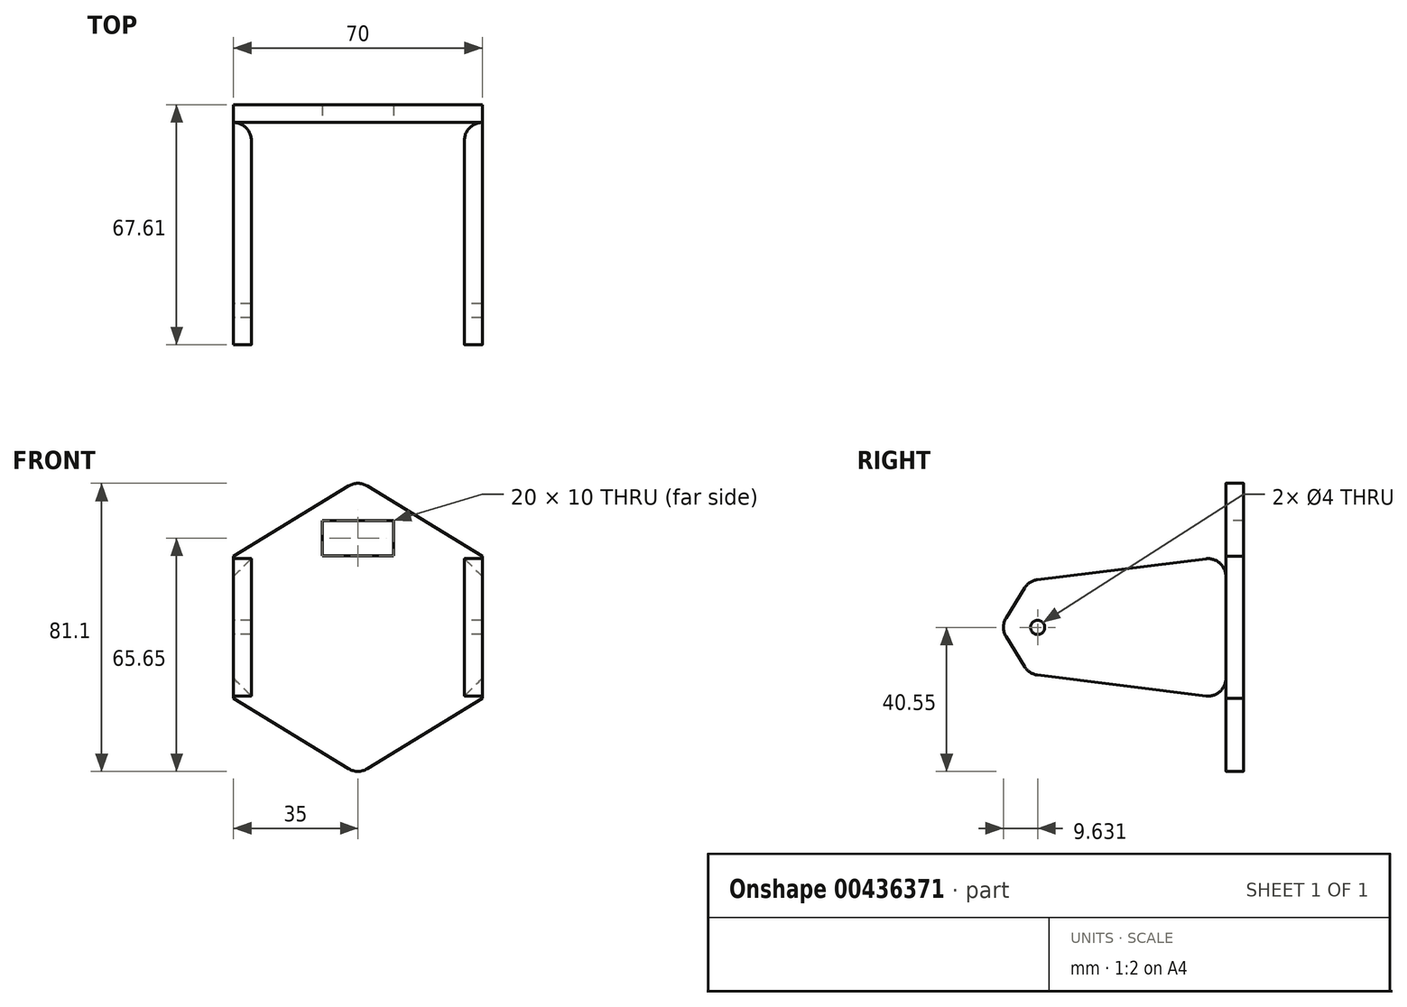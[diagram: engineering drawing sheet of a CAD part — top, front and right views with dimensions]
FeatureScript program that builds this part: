
annotation { "Feature Type Name" : "Feature", "Feature Type Description" : "" }
export const myFeature = defineFeature(function(context is Context, id is Id, definition is map)
    precondition{}
    {
        {
            var Q0;
            Q0=qCreatedBy(makeId("Front.planeOp"),FACE);
            var sketch = newSketch(context, id + "F0", { "sketchPlane" : qUnion([Q0])});
            skLineSegment(sketch, "E0.bottom", {"start": v(-35, 20) * mm, "end": v(-30, 20) * mm});
            skLineSegment(sketch, "E0.top", {"start": v(-35, -20) * mm, "end": v(-30, -20) * mm});
            skLineSegment(sketch, "E0.left", {"start": v(-35, 20) * mm, "end": v(-35, -20) * mm});
            skLineSegment(sketch, "E0.right", {"start": v(-30, 20) * mm, "end": v(-30, -20) * mm});
            skLineSegment(sketch, "E1.MirrorCS", {"start": v(35, 20) * mm, "end": v(30, 20) * mm});
            skLineSegment(sketch, "E2.MirrorCS", {"start": v(35, -20) * mm, "end": v(30, -20) * mm});
            skLineSegment(sketch, "E3.MirrorCS", {"start": v(30, 20) * mm, "end": v(30, -20) * mm});
            skLineSegment(sketch, "E4.MirrorCS", {"start": v(35, 20) * mm, "end": v(35, -20) * mm});
            skSolve(sketch);
        }
        {
            var Q0;
            Q0 = qSketchRegion(id + "F0", true);
            extrude(context, id + "F1", {"entities" : qUnion([Q0]), "depth" : 70 * mm});
        }
        {
            var Q0;
            Q0=makeQuery(id+"F1.opExtrude","CAP_FACE",FACE,{"disambiguationData":[OSD([sQuery(id+"F0.wireOp",EDGE,"E0.bottom"),sQuery(id+"F0.wireOp",EDGE,"E0.top"),sQuery(id+"F0.wireOp",EDGE,"E0.left"),sQuery(id+"F0.wireOp",EDGE,"E0.right")])],"isStart":true});
            var sketch = newSketch(context, id + "F2", { "sketchPlane" : qUnion([Q0])});
            skLineSegment(sketch, "E5", {"start": v(0, -41.41) * mm, "end": v(35, -20) * mm});
            skLineSegment(sketch, "E6.0", {"start": v(35, 20) * mm, "end": v(35, -20) * mm});
            skLineSegment(sketch, "E7.0", {"start": v(-35, 20) * mm, "end": v(-35, -20) * mm});
            skLineSegment(sketch, "E8.MirrorCS", {"start": v(0, -41.41) * mm, "end": v(-35, -20) * mm});
            skLineSegment(sketch, "E9.MirrorCS", {"start": v(0, 41.41) * mm, "end": v(35, 20) * mm});
            skLineSegment(sketch, "E10.MirrorCS", {"start": v(0, 41.41) * mm, "end": v(-35, 20) * mm});
            skSolve(sketch);
        }
        {
            var Q0;
            Q0 = qSketchRegion(id + "F2", true);
            extrude(context, id + "F3", {"entities" : qUnion([Q0]), "depth" : 5 * mm});
        }
        {
            var Q0;
            Q0=makeQuery(id+"F1.opExtrude","SWEPT_FACE",FACE,{"disambiguationData":[OSD([sQuery(id+"F0.wireOp",EDGE,"E0.left")])]});
            var sketch = newSketch(context, id + "F4", { "sketchPlane" : qUnion([Q0])});
            skCircle(sketch, "E11", {"center": v(52.98, 0) * mm, "radius": 2 * mm});
            skSolve(sketch);
        }
        {
            var Q0;
            Q0 = qSketchRegion(id + "F4", true);
            extrude(context, id + "F5", {"entities" : qUnion([Q0]), "operationType" : NewBodyOperationType.REMOVE, "oppositeDirection" : true, "depth" : 97.2 * mm});
        }
        {
            var Q0;
            Q0=makeQuery(id+"F1.opExtrude","SWEPT_FACE",FACE,{"disambiguationData":[OSD([sQuery(id+"F0.wireOp",EDGE,"E0.left")])]});
            var sketch = newSketch(context, id + "F6", { "sketchPlane" : qUnion([Q0])});
            skLineSegment(sketch, "E12", {"start": v(0, 20) * mm, "end": v(53.02, 13.43) * mm});
            skLineSegment(sketch, "E13", {"start": v(56.66, 11.08) * mm, "end": v(61.87, 2.62) * mm});
            skLineSegment(sketch, "E14.MirrorCS", {"start": v(56.66, -11.08) * mm, "end": v(61.87, -2.62) * mm});
            skLineSegment(sketch, "E15.MirrorCS", {"start": v(0, -20) * mm, "end": v(53.02, -13.43) * mm});
            skPoint(sketch, "E16.visualSharp", {"position": v(63.48, 0) * mm});
            skArc(sketch, "E16.filletArc", {"start": v(61.87, -2.62) * mm, "mid": v(62.61, 0) * mm, "end": v(61.87, 2.62) * mm});
            skPoint(sketch, "E17.visualSharp", {"position": v(55.4, 13.13) * mm});
            skArc(sketch, "E17.filletArc", {"start": v(56.66, 11.08) * mm, "mid": v(55.1, 12.67) * mm, "end": v(53.02, 13.43) * mm});
            skPoint(sketch, "E18.visualSharp", {"position": v(55.4, -13.13) * mm});
            skArc(sketch, "E18.filletArc", {"start": v(53.02, -13.43) * mm, "mid": v(55.1, -12.67) * mm, "end": v(56.66, -11.08) * mm});
            skLineSegment(sketch, "E19", {"start": v(0, 20) * mm, "end": v(98.43, 40.8) * mm});
            skLineSegment(sketch, "E20", {"start": v(98.43, 40.8) * mm, "end": v(98.43, -42.02) * mm});
            skLineSegment(sketch, "E21", {"start": v(98.43, -42.02) * mm, "end": v(0, -20) * mm});
            skSolve(sketch);
        }
        {
            var Q0;
            Q0 = qSketchRegion(id + "F6", true);
            extrude(context, id + "F7", {"entities" : qUnion([Q0]), "operationType" : NewBodyOperationType.REMOVE, "oppositeDirection" : true, "depth" : 83.6 * mm});
        }
        {
            var Q0;
            Q0=makeQuery(id+"F3.opExtrude","SWEPT_EDGE",EDGE,{"disambiguationData":[OSD([sQuery(id+"F2.wireOp",EDGE,"E9.MirrorCS"),sQuery(id+"F2.wireOp",EDGE,"E10.MirrorCS")])]});
            var Q1;
            Q1=makeQuery(id+"F1.opExtrude","CAP_EDGE",EDGE,{"disambiguationData":[OSD([sQuery(id+"F0.wireOp",EDGE,"E3.MirrorCS")])],"isStart":true});
            var Q2;
            Q2=makeQuery(id+"F1.opExtrude","CAP_EDGE",EDGE,{"disambiguationData":[OSD([sQuery(id+"F0.wireOp",EDGE,"E0.right")])],"isStart":true});
            var Q3;
            Q3=makeQuery(id+"F3.opExtrude","SWEPT_EDGE",EDGE,{"disambiguationData":[OSD([sQuery(id+"F2.wireOp",EDGE,"E5"),sQuery(id+"F2.wireOp",EDGE,"E8.MirrorCS")])]});
            var Q4;
            Q4=makeQuery(id+"F7.boolean.opBoolean","MERGE",EDGE,{"derivedFrom":[makeQuery(id+"F1.opExtrude","CAP_EDGE",EDGE,{"disambiguationData":[OSD([sQuery(id+"F0.wireOp",EDGE,"E1.MirrorCS")])],"isStart":true}),makeQuery(id+"F7.opExtrude","SWEPT_EDGE",EDGE,{"disambiguationData":[OSD([sQuery(id+"F0.wireOp",EDGE,"E0.bottom"),sQuery(id+"F0.wireOp",EDGE,"E0.left"),sQuery(id+"F6.wireOp",EDGE,"E12"),sQuery(id+"F6.wireOp",EDGE,"E19")])]})]});
            var Q5;
            {var subQ0=sQuery(id+"F0.wireOp",EDGE,"E0.bottom");Q5=makeQuery(id+"F7.boolean.opBoolean","MERGE",EDGE,{"derivedFrom":[makeQuery(id+"F1.opExtrude","CAP_EDGE",EDGE,{"disambiguationData":[OSD([subQ0])],"isStart":true}),makeQuery(id+"F7.opExtrude","SWEPT_EDGE",EDGE,{"disambiguationData":[OSD([subQ0,sQuery(id+"F0.wireOp",EDGE,"E0.left"),sQuery(id+"F6.wireOp",EDGE,"E12"),sQuery(id+"F6.wireOp",EDGE,"E19")])]})]});}
            var Q6;
            {var subQ0=sQuery(id+"F0.wireOp",EDGE,"E0.top");Q6=makeQuery(id+"F7.boolean.opBoolean","MERGE",EDGE,{"derivedFrom":[makeQuery(id+"F1.opExtrude","CAP_EDGE",EDGE,{"disambiguationData":[OSD([subQ0])],"isStart":true}),makeQuery(id+"F7.opExtrude","SWEPT_EDGE",EDGE,{"disambiguationData":[OSD([subQ0,sQuery(id+"F0.wireOp",EDGE,"E0.left"),sQuery(id+"F6.wireOp",EDGE,"E15.MirrorCS"),sQuery(id+"F6.wireOp",EDGE,"E21")])]})]});}
            var Q7;
            Q7=makeQuery(id+"F7.boolean.opBoolean","MERGE",EDGE,{"derivedFrom":[makeQuery(id+"F1.opExtrude","CAP_EDGE",EDGE,{"disambiguationData":[OSD([sQuery(id+"F0.wireOp",EDGE,"E2.MirrorCS")])],"isStart":true}),makeQuery(id+"F7.opExtrude","SWEPT_EDGE",EDGE,{"disambiguationData":[OSD([sQuery(id+"F0.wireOp",EDGE,"E0.top"),sQuery(id+"F0.wireOp",EDGE,"E0.left"),sQuery(id+"F6.wireOp",EDGE,"E15.MirrorCS"),sQuery(id+"F6.wireOp",EDGE,"E21")])]})]});
            fillet(context, id + "F8", {"entities" : qUnion([Q0, Q1, Q2, Q3, Q4, Q5, Q6, Q7]), "radius" : 5 * mm, "tangentPropagation" : true, "allowEdgeOverflow" : false});
        }
        {
            var Q0;
            Q0=makeQuery(id+"F3.opExtrude","CAP_FACE",FACE,{"disambiguationData":[OSD([sQuery(id+"F2.wireOp",EDGE,"E5"),sQuery(id+"F2.wireOp",EDGE,"E6.0"),sQuery(id+"F2.wireOp",EDGE,"E7.0"),sQuery(id+"F2.wireOp",EDGE,"E8.MirrorCS"),sQuery(id+"F2.wireOp",EDGE,"E9.MirrorCS"),sQuery(id+"F2.wireOp",EDGE,"E10.MirrorCS")])],"isStart":true});
            var sketch = newSketch(context, id + "F9", { "sketchPlane" : qUnion([Q0])});
            skLineSegment(sketch, "E22.bottom", {"start": v(-10, 30.1) * mm, "end": v(10, 30.1) * mm});
            skLineSegment(sketch, "E22.top", {"start": v(-10, 20.1) * mm, "end": v(10, 20.1) * mm});
            skLineSegment(sketch, "E22.left", {"start": v(-10, 30.1) * mm, "end": v(-10, 20.1) * mm});
            skLineSegment(sketch, "E22.right", {"start": v(10, 30.1) * mm, "end": v(10, 20.1) * mm});
            skSolve(sketch);
        }
        {
            var Q0;
            Q0 = qSketchRegion(id + "F9", true);
            extrude(context, id + "F10", {"entities" : qUnion([Q0]), "operationType" : NewBodyOperationType.REMOVE, "oppositeDirection" : true, "depth" : 25 * mm});
        }
    });
